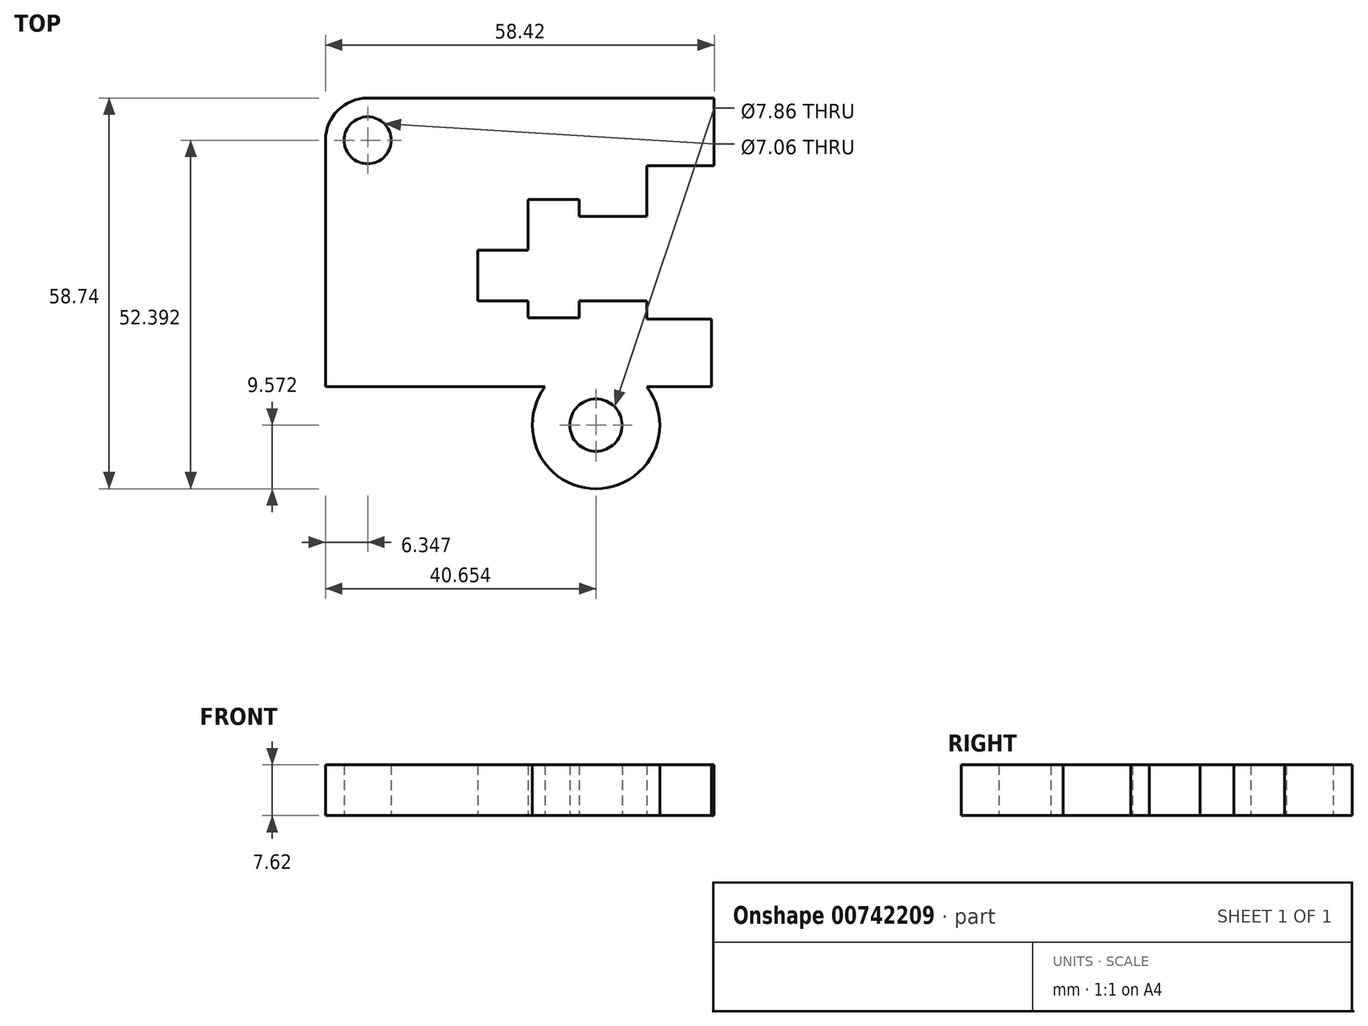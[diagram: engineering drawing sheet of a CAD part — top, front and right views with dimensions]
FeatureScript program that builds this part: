
annotation { "Feature Type Name" : "Feature", "Feature Type Description" : "" }
export const myFeature = defineFeature(function(context is Context, id is Id, definition is map)
    precondition{}
    {
        {
            var Q0;
            Q0=qCreatedBy(makeId("Top.planeOp"),FACE);
            var sketch = newSketch(context, id + "F0", { "sketchPlane" : qUnion([Q0])});
            skLineSegment(sketch, "E0", {"start": v(-51.64, 33.24) * mm, "end": v(0.43, 33.24) * mm});
            skLineSegment(sketch, "E1", {"start": v(0.43, 33.24) * mm, "end": v(0.43, 23.08) * mm});
            skLineSegment(sketch, "E2", {"start": v(0.43, 23.08) * mm, "end": v(-9.73, 23.08) * mm});
            skLineSegment(sketch, "E3", {"start": v(-9.73, 23.08) * mm, "end": v(-9.73, 15.46) * mm});
            skLineSegment(sketch, "E4", {"start": v(-9.73, 15.46) * mm, "end": v(-19.9, 15.46) * mm});
            skLineSegment(sketch, "E5", {"start": v(-19.9, 15.46) * mm, "end": v(-19.9, 18) * mm});
            skLineSegment(sketch, "E6", {"start": v(-19.9, 18) * mm, "end": v(-27.51, 18) * mm});
            skLineSegment(sketch, "E7", {"start": v(-27.51, 18) * mm, "end": v(-27.51, 10.38) * mm});
            skLineSegment(sketch, "E8", {"start": v(-27.51, 10.38) * mm, "end": v(-35.13, 10.38) * mm});
            skLineSegment(sketch, "E9", {"start": v(-35.13, 10.38) * mm, "end": v(-35.13, 2.76) * mm});
            skLineSegment(sketch, "E10", {"start": v(-35.13, 2.76) * mm, "end": v(-27.51, 2.76) * mm});
            skLineSegment(sketch, "E11", {"start": v(-27.51, 2.76) * mm, "end": v(-27.51, 0.22) * mm});
            skLineSegment(sketch, "E12", {"start": v(-27.51, 0.22) * mm, "end": v(-19.9, 0.22) * mm});
            skLineSegment(sketch, "E13", {"start": v(-19.9, 0.22) * mm, "end": v(-19.9, 2.76) * mm});
            skLineSegment(sketch, "E14", {"start": v(-19.9, 2.76) * mm, "end": v(-9.73, 2.76) * mm});
            skLineSegment(sketch, "E15", {"start": v(-9.73, 2.76) * mm, "end": v(-9.73, 0) * mm});
            skLineSegment(sketch, "E16", {"start": v(-9.73, 0) * mm, "end": v(0, 0) * mm});
            skLineSegment(sketch, "E17", {"start": v(0, 0) * mm, "end": v(0, -10.16) * mm});
            skLineSegment(sketch, "E18", {"start": v(-58, -10.16) * mm, "end": v(-58, 26.9) * mm});
            skPoint(sketch, "E19.visualSharp", {"position": v(-58, 33.24) * mm});
            skArc(sketch, "E19.filletArc", {"start": v(-51.64, 33.24) * mm, "mid": v(-56.13, 31.38) * mm, "end": v(-58, 26.9) * mm});
            skLineSegment(sketch, "E20", {"start": v(-58, -10.16) * mm, "end": v(-24.97, -10.16) * mm});
            skLineSegment(sketch, "E21", {"start": v(-9.7, -10.16) * mm, "end": v(0, -10.16) * mm});
            skArc(sketch, "E22", {"start": v(-24.97, -10.16) * mm, "mid": v(-17.34, -25.5) * mm, "end": v(-9.7, -10.16) * mm});
            skCircle(sketch, "E23", {"center": v(-17.34, -15.93) * mm, "radius": 3.93 * mm});
            skCircle(sketch, "E24", {"center": v(-51.64, 26.9) * mm, "radius": 3.53 * mm});
            skSolve(sketch);
        }
        {
            var Q0;
            Q0 = qSketchRegion(id + "F0", true);
            extrude(context, id + "F1", {"entities" : qUnion([Q0]), "depth" : 7.62 * mm, "offsetDistance" : 25.4 * mm});
        }
    });
